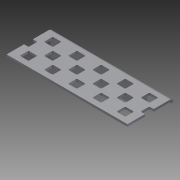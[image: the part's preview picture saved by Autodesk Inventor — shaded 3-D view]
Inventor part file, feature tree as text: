
AUTODESK INVENTOR PART (.ipt)
format: ipt  version: 2012 (Build 160160000, 160)  size: 827,904 bytes
history: native  units: in
note: dims shown in document units (in); Inventor stores cm internally (conversion verified against a paired STEP export)
features: plane x2, split x2, other x1, imported_body x1, extrude x1, sketch x1
ambient origin geometry x8: Origin, YZ Plane, XZ Plane, XY Plane, X Axis, Y Axis, Z Axis, Center Point
feature tree (8):
  parser-record x1  (decoder bookkeeping rows leaked as tree rows — omitted from the tree; the rows remain in map.json)
  imported_body  "Base1"
  plane  "Work Plane1"
  split  "Split1"
  plane  "Work Plane2"
  split  "Split2"
  extrude  "Extrusion1"  [1 undecoded]
  sketch  "Sketch1"  dims[d0=-1.0in d1=-9.0in d2=1.0in d3=0.0in]
note: 1 required parameter value undecoded (feature->parameter linkage not recoverable at this tier; creation-order binding heuristic only, values carry confidence <= 0.55)
